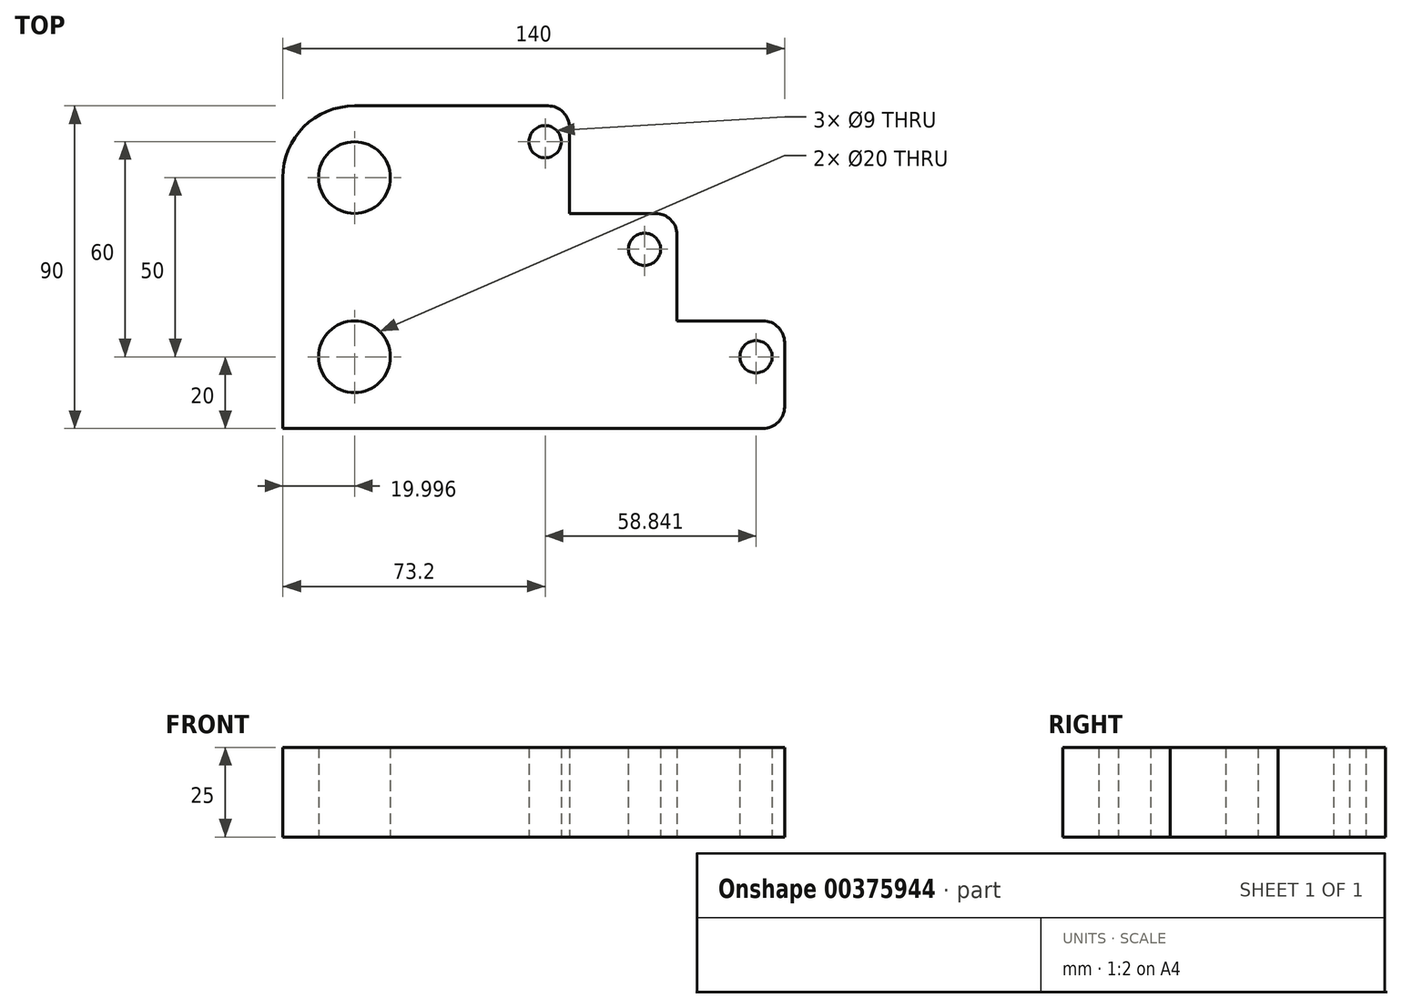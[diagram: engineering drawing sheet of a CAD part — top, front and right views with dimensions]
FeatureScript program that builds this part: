
annotation { "Feature Type Name" : "Feature", "Feature Type Description" : "" }
export const myFeature = defineFeature(function(context is Context, id is Id, definition is map)
    precondition{}
    {
        {
            var Q0;
            Q0=qCreatedBy(makeId("Top.planeOp"),FACE);
            var sketch = newSketch(context, id + "F0", { "sketchPlane" : qUnion([Q0])});
            skLineSegment(sketch, "E0", {"start": v(-85.2, 34.13) * mm, "end": v(-85.2, -15.87) * mm});
            skLineSegment(sketch, "E1", {"start": v(-65.2, -35.87) * mm, "end": v(48.8, -35.87) * mm});
            skLineSegment(sketch, "E2", {"start": v(54.8, -29.87) * mm, "end": v(54.8, -11.87) * mm});
            skLineSegment(sketch, "E3", {"start": v(48.8, -5.87) * mm, "end": v(24.8, -5.87) * mm});
            skLineSegment(sketch, "E4", {"start": v(24.8, -5.87) * mm, "end": v(24.8, 18.13) * mm});
            skLineSegment(sketch, "E5", {"start": v(18.8, 24.13) * mm, "end": v(-5.2, 24.13) * mm});
            skLineSegment(sketch, "E6", {"start": v(-5.2, 24.13) * mm, "end": v(-5.2, 48.13) * mm});
            skLineSegment(sketch, "E7", {"start": v(-11.2, 54.13) * mm, "end": v(-65.2, 54.13) * mm});
            skPoint(sketch, "E8.visualSharp", {"position": v(54.8, -35.87) * mm});
            skArc(sketch, "E8.filletArc", {"start": v(48.8, -35.87) * mm, "mid": v(53.04, -34.11) * mm, "end": v(54.8, -29.87) * mm});
            skPoint(sketch, "E9.visualSharp", {"position": v(-85.2, 54.13) * mm});
            skArc(sketch, "E9.filletArc", {"start": v(-65.2, 54.13) * mm, "mid": v(-79.35, 48.27) * mm, "end": v(-85.2, 34.13) * mm});
            skPoint(sketch, "E10.visualSharp", {"position": v(-85.2, -35.87) * mm});
            skArc(sketch, "E10.filletArc", {"start": v(-85.2, -15.87) * mm, "mid": v(-79.35, -30.01) * mm, "end": v(-65.2, -35.87) * mm});
            skPoint(sketch, "E11.visualSharp", {"position": v(-5.2, 54.13) * mm});
            skArc(sketch, "E11.filletArc", {"start": v(-5.2, 48.13) * mm, "mid": v(-6.96, 52.37) * mm, "end": v(-11.2, 54.13) * mm});
            skPoint(sketch, "E12.visualSharp", {"position": v(24.8, 24.13) * mm});
            skArc(sketch, "E12.filletArc", {"start": v(24.8, 18.13) * mm, "mid": v(23.04, 22.37) * mm, "end": v(18.8, 24.13) * mm});
            skPoint(sketch, "E13.visualSharp", {"position": v(54.8, -5.87) * mm});
            skArc(sketch, "E13.filletArc", {"start": v(54.8, -11.87) * mm, "mid": v(53.04, -7.63) * mm, "end": v(48.8, -5.87) * mm});
            skCircle(sketch, "E14", {"center": v(46.84, -15.87) * mm, "radius": 4.5 * mm});
            skCircle(sketch, "E15", {"center": v(15.72, 14.13) * mm, "radius": 4.5 * mm});
            skCircle(sketch, "E16", {"center": v(-12, 44.13) * mm, "radius": 4.5 * mm});
            skLineSegment(sketch, "E17", {"start": v(-85.2, 34.13) * mm, "end": v(-85.2, -35.87) * mm});
            skLineSegment(sketch, "E18", {"start": v(-85.2, -35.87) * mm, "end": v(-65.2, -35.87) * mm});
            skLineSegment(sketch, "E19", {"start": v(-85.2, -35.87) * mm, "end": v(-85.2, -15.87) * mm});
            skCircle(sketch, "E20", {"center": v(-65.2, -15.87) * mm, "radius": 10 * mm});
            skCircle(sketch, "E21", {"center": v(-65.2, 34.13) * mm, "radius": 10 * mm});
            skSolve(sketch);
        }
        {
            var Q0;
            Q0 = qSketchRegion(id + "F0", true);
            extrude(context, id + "F1", {"entities" : qUnion([Q0]), "depth" : 25 * mm});
        }
    });
